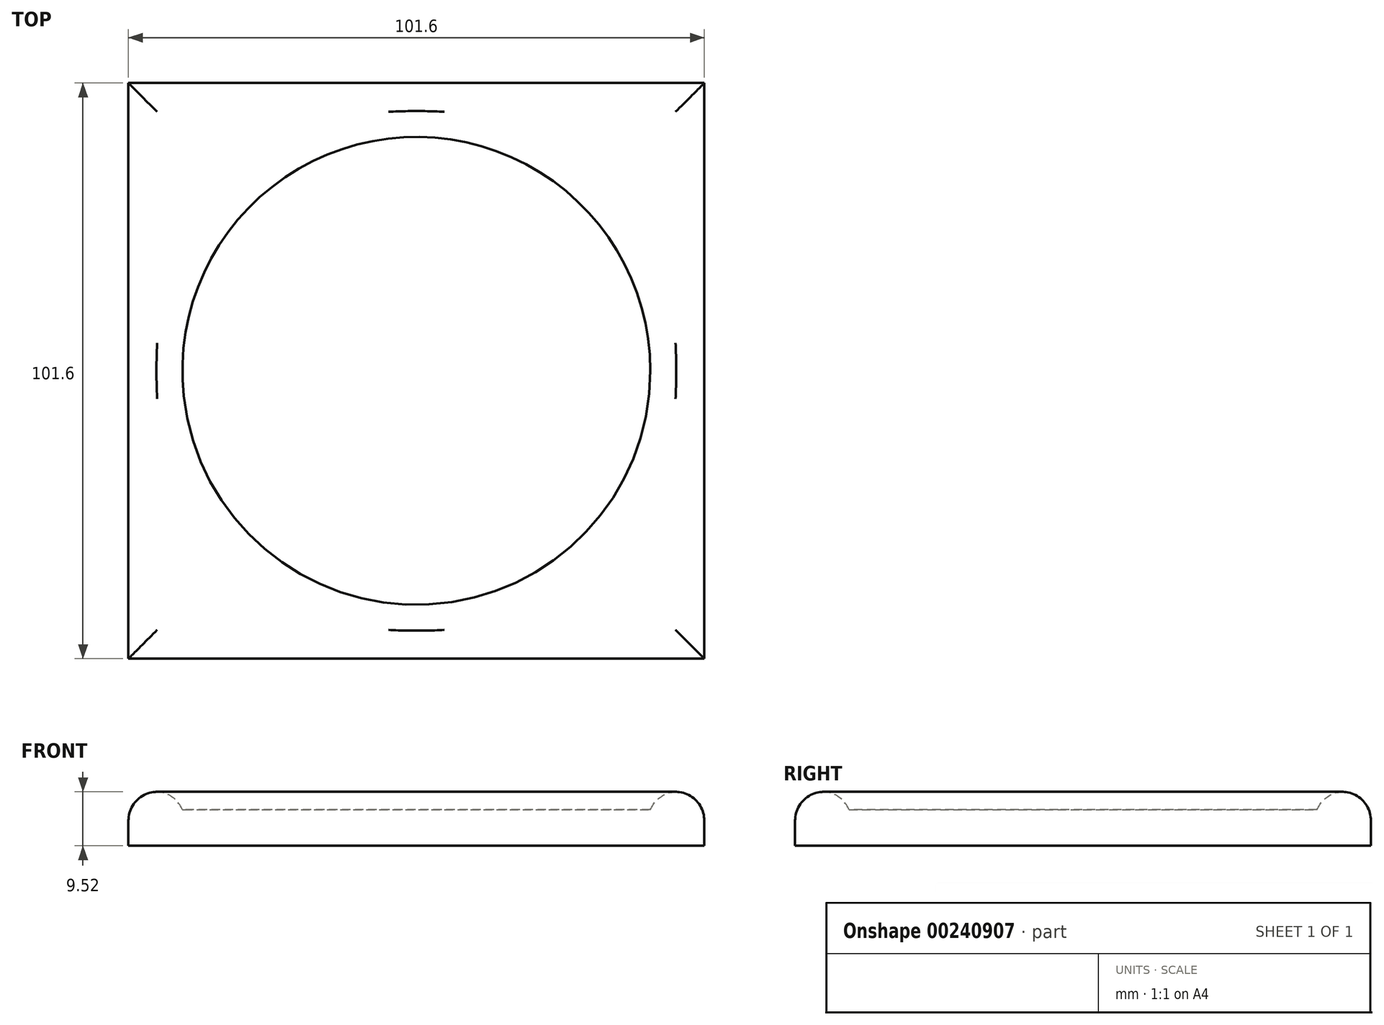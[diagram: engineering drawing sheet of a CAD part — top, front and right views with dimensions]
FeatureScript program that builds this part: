
annotation { "Feature Type Name" : "Feature", "Feature Type Description" : "" }
export const myFeature = defineFeature(function(context is Context, id is Id, definition is map)
    precondition{}
    {
        {
            var Q0;
            Q0=qCreatedBy(makeId("Front.planeOp"),FACE);
            var sketch = newSketch(context, id + "F0", { "sketchPlane" : qUnion([Q0])});
            skLineSegment(sketch, "E0.bottom", {"start": v(50.8, 4.76) * mm, "end": v(-50.8, 4.76) * mm});
            skLineSegment(sketch, "E0.top", {"start": v(50.8, -4.76) * mm, "end": v(-50.8, -4.76) * mm});
            skLineSegment(sketch, "E0.left", {"start": v(50.8, 4.76) * mm, "end": v(50.8, -4.76) * mm});
            skLineSegment(sketch, "E0.right", {"start": v(-50.8, 4.76) * mm, "end": v(-50.8, -4.76) * mm});
            skPoint(sketch, "E0.middle", {"position": v(0, 0) * mm});
            skSolve(sketch);
        }
        {
            var Q0;
            Q0 = qSketchRegion(id + "F0", true);
            extrude(context, id + "F1", {"entities" : qUnion([Q0]), "endBound" : BoundingType.SYMMETRIC, "depth" : 101.6 * mm});
        }
        {
            var Q0;
            Q0=makeQuery(id+"F1.opExtrude","SWEPT_FACE",FACE,{"disambiguationData":[OSD([sQuery(id+"F0.wireOp",EDGE,"E0.bottom")])]});
            var sketch = newSketch(context, id + "F2", { "sketchPlane" : qUnion([Q0])});
            skCircle(sketch, "E1", {"center": v(0, 0) * mm, "radius": 41.28 * mm});
            skSolve(sketch);
        }
        {
            var Q0;
            Q0 = qSketchRegion(id + "F2", true);
            extrude(context, id + "F3", {"entities" : qUnion([Q0]), "operationType" : NewBodyOperationType.REMOVE, "oppositeDirection" : true, "depth" : 3.17 * mm});
        }
        {
            var Q0;
            Q0=makeQuery(id+"F1.opExtrude","CAP_EDGE",EDGE,{"disambiguationData":[OSD([sQuery(id+"F0.wireOp",EDGE,"E0.bottom")])],"isStart":true});
            var Q1;
            Q1=makeQuery(id+"F1.opExtrude","SWEPT_FACE",FACE,{"disambiguationData":[OSD([sQuery(id+"F0.wireOp",EDGE,"E0.bottom")])]});
            fillet(context, id + "F4", {"entities" : qUnion([Q0, Q1]), "radius" : 5.08 * mm, "tangentPropagation" : true, "allowEdgeOverflow" : false});
        }
    });
